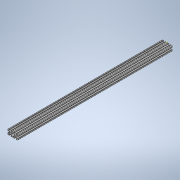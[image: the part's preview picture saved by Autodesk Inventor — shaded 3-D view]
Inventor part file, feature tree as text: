
AUTODESK INVENTOR PART (.ipt)
format: ipt  version: 2020 (Build 240168000, 168)  size: 336,384 bytes
history: native  units: in
note: dims shown in document units (in); Inventor stores cm internally (conversion verified against a paired STEP export)
features: sketch x2, extrude x1
ambient origin geometry x8: Origin, YZ Plane, XZ Plane, XY Plane, X Axis, Y Axis, Z Axis, Center Point
bodies: Solid1 (feature_tree)
feature tree (3):
  extrude  "Extrusion1"  [1 undecoded]
  sketch  "Sketch2"
  sketch  "Sketch1"  dims[d0=30.0in d1=0.0in]
note: 1 required parameter value undecoded (feature->parameter linkage not recoverable at this tier; creation-order binding heuristic only, values carry confidence <= 0.55)
